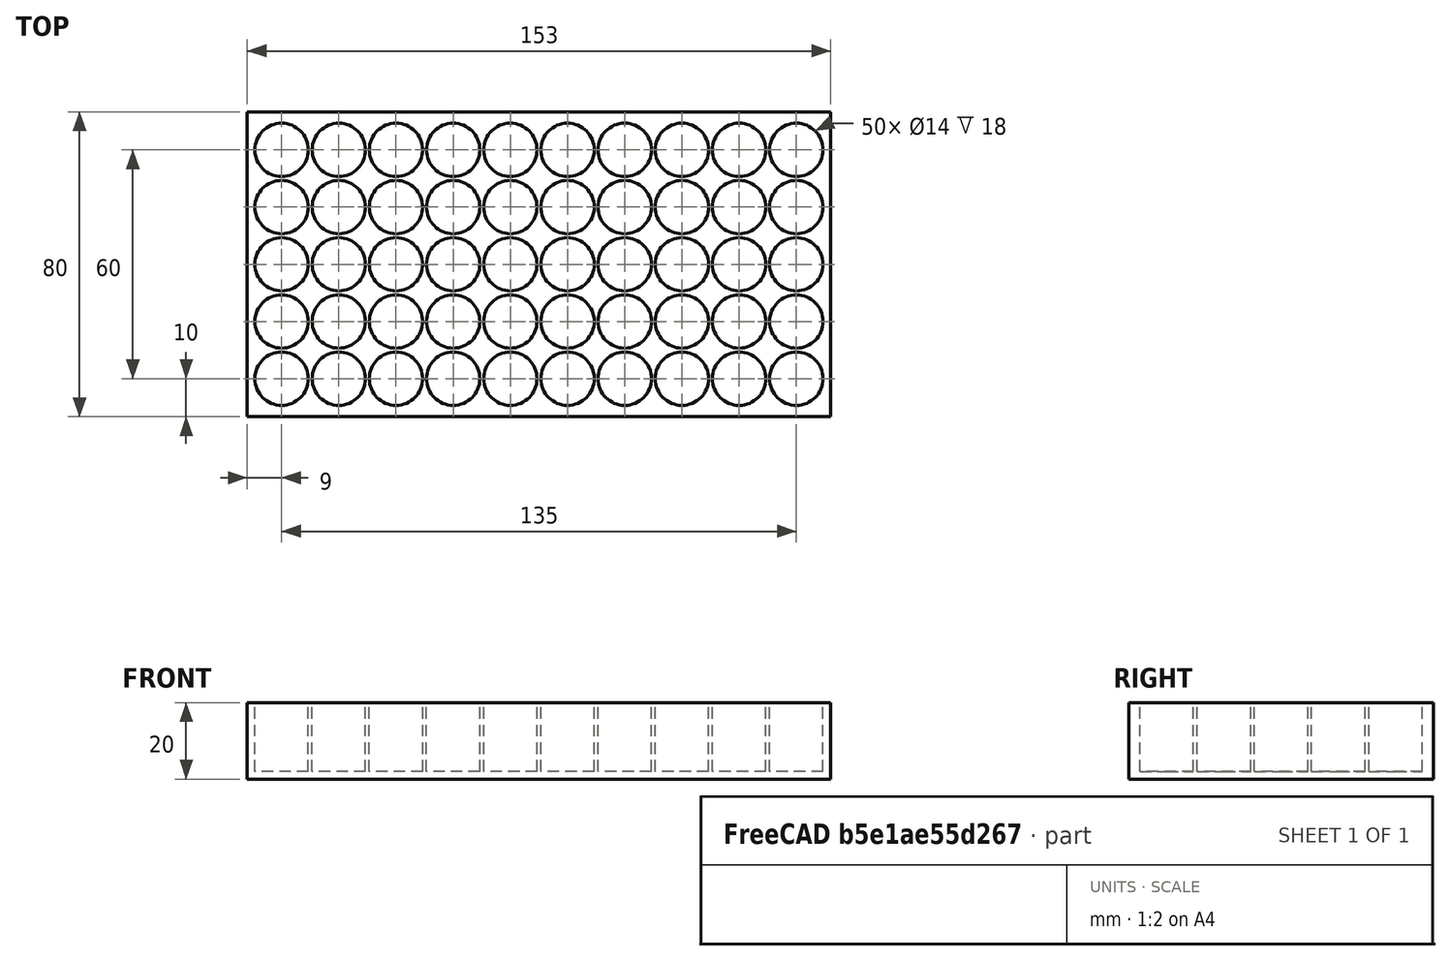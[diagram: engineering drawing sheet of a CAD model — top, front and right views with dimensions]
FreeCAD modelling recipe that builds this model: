
FCSTD DOCUMENT  (FreeCAD 0.16R6707 (Git))
Label: Soporte_pilas-AAA_10x5
License: CC-BY 3.0
LicenseURL: http://creativecommons.org/licenses/by/3.0/
objects: Part::Cylinder×1, Part::FeaturePython×1, Part::Box×1, Part::Cut×1
note: 4 computed .brp shape members not serialized (recipe doc carries the construction recipe); baked Part::Feature solids carry a one-line shape summary decoded from their .brp

FEATURE [Part::Cylinder] Cylinder  label="Hueco_pilas"
  Angle = 360
  Height = 20
  Placement = pos=(0,0,2) rot=(0,0,1;0rad)
  Radius = 7
FEATURE [Part::FeaturePython] Array  label="ConjuntoPilas"  # Draft array (typed FeaturePython)
  Angle = 360
  ArrayType = 0
  Axis = (0,0,1)
  Base = -> Cylinder
  Center = (0,0,0)
  IntervalX = (15,0,0)
  IntervalY = (0,15,0)
  IntervalZ = (0,0,1)
  NumberPolar = 1
  NumberX = 10
  NumberY = 5
  NumberZ = 1
FEATURE [Part::Box] Box  label="Base"
  Height = 20
  Length = 153
  Placement = pos=(-9,-10,0) rot=(0,0,1;0rad)
  Width = 80
FEATURE [Part::Cut] Cut  label="SoportePilas"
  Base = -> Box
  Tool = -> Array
